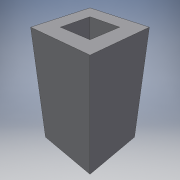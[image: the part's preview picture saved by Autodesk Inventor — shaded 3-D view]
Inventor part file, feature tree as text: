
AUTODESK INVENTOR PART (.ipt)
format: ipt  version: 2016 (Build 200138000, 138)  size: 107,008 bytes
history: native  units: in
note: dims shown in document units (in); Inventor stores cm internally (conversion verified against a paired STEP export)
features: extrude x3, sketch x3
ambient origin geometry x8: Origin, YZ Plane, XZ Plane, XY Plane, X Axis, Y Axis, Z Axis, Center Point
bodies: Solid1 (feature_tree)
feature tree (6):
  extrude  "Extrusion1"  Depth=3.0in
  extrude  "Extrusion2"  Depth=0.75in TaperAngle=0.0deg
  extrude  "Extrusion3"  Depth=1.5in
  sketch  "Sketch1"  dims[d0=5.5in d1=3.0in]
  sketch  "Sketch2"  dims[d6=1.5in d7=0.0in d8=0.75in d9=0.0in]
  sketch  "Sketch3"  dims[d10=0.75in d11=0.0in d13=1.5in]
